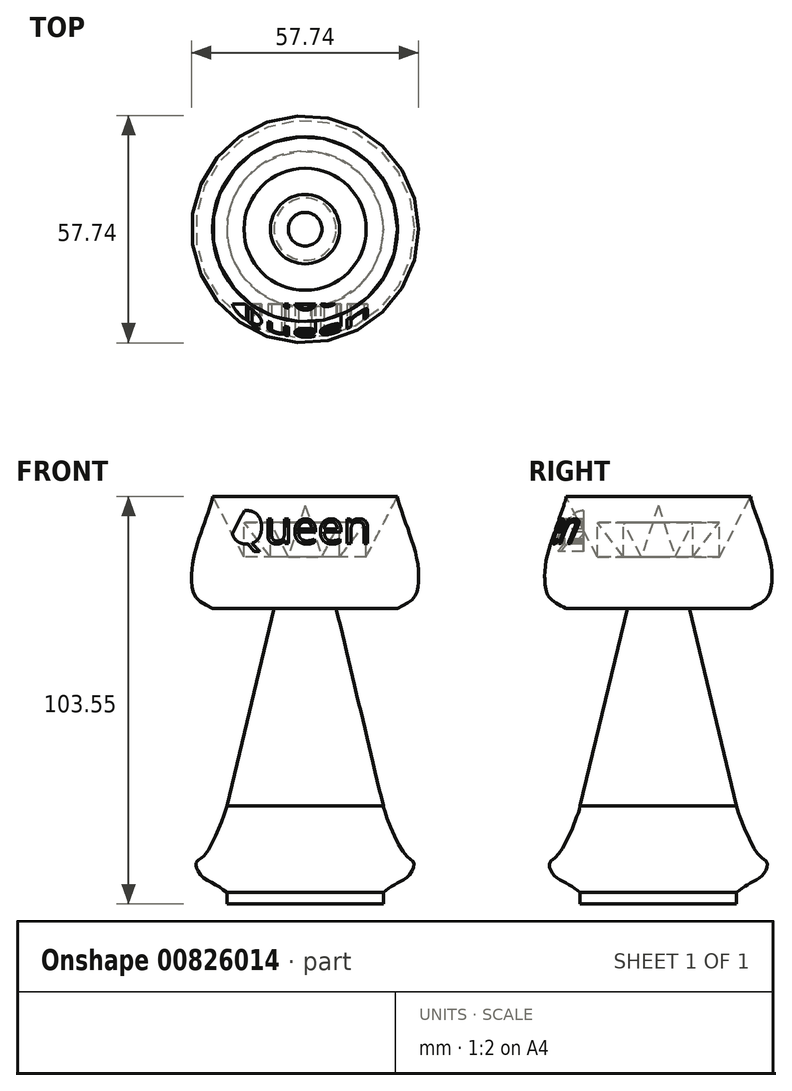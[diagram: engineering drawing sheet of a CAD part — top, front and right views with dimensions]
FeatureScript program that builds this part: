
annotation { "Feature Type Name" : "Feature", "Feature Type Description" : "" }
export const myFeature = defineFeature(function(context is Context, id is Id, definition is map)
    precondition{}
    {
        {
            var Q0;
            Q0=qCreatedBy(makeId("Front.planeOp"),FACE);
            var sketch = newSketch(context, id + "F0", { "sketchPlane" : qUnion([Q0])});
            skLineSegment(sketch, "E0", {"start": v(0, 46) * mm, "end": v(0, -55.25) * mm});
            skLineSegment(sketch, "E1", {"start": v(0, -55.25) * mm, "end": v(19.87, -55.25) * mm});
            skLineSegment(sketch, "E2", {"start": v(19.87, -55.25) * mm, "end": v(19.87, -52.35) * mm});
            skFitSpline(sketch, "E3", {"points": [v(19.87, -52.35) * mm, v(21.86, -50.9) * mm, v(24.04, -49.63) * mm, v(26.58, -47.81) * mm, v(27.67, -44.9) * mm, v(25.31, -42.55) * mm, v(19.87, -30.57) * mm, v(19.87, -30.4) * mm], "startDerivative": vector(15.77, 12.02) * mm, "endDerivative": vector(1.1, 2.52) * mm});
            skLineSegment(sketch, "E4", {"start": v(19.87, -30.4) * mm, "end": v(7.9, 19.87) * mm});
            skLineSegment(sketch, "E5", {"start": v(7.9, 19.87) * mm, "end": v(23.5, 19.87) * mm});
            skFitSpline(sketch, "E6", {"points": [v(23.5, 19.87) * mm, v(27.49, 22.4) * mm, v(28.76, 25.86) * mm, v(28.58, 31.48) * mm, v(26.95, 37.65) * mm, v(24.95, 43.28) * mm, v(23.5, 47.81) * mm, v(23.5, 48.18) * mm, v(23.5, 48.36) * mm], "startDerivative": vector(31.12, 15.03) * mm, "endDerivative": vector(-0.24, 6.22) * mm});
            skLineSegment(sketch, "E7", {"start": v(23.5, 48.3) * mm, "end": v(15.51, 32.93) * mm});
            skLineSegment(sketch, "E8", {"start": v(15.51, 32.93) * mm, "end": v(15.51, 41.64) * mm});
            skLineSegment(sketch, "E9", {"start": v(15.51, 41.64) * mm, "end": v(8.8, 32.93) * mm});
            skLineSegment(sketch, "E10", {"start": v(8.8, 32.93) * mm, "end": v(8.8, 41.64) * mm});
            skLineSegment(sketch, "E11", {"start": v(8.8, 41.64) * mm, "end": v(4.27, 32.93) * mm});
            skLineSegment(sketch, "E12", {"start": v(4.27, 32.93) * mm, "end": v(0, 46) * mm});
            skSolve(sketch);
        }
        {
            var Q0;
            Q0 = qSketchRegion(id + "F0", true);
            var Q1;
            Q1=sQuery(id+"F0.wireOp",EDGE,"E0");
            revolve(context, id + "F1", {"surfaceOperationType" : NewSurfaceOperationType.NEW, "entities" : qUnion([Q0]), "axis" : qUnion([Q1]), "revolveType" : RevolveType.FULL});
        }
        {
            var Q0;
            Q0=qCreatedBy(makeId("Front.planeOp"),FACE);
            cPlane(context, id + "F2", {"entities" : qUnion([Q0]), "cplaneType" : CPlaneType.OFFSET, "offset" : 38.8 * mm, "width" : 150 * mm, "height" : 150 * mm});
        }
        {
            var Q0;
            Q0=qCreatedBy(id+"F2.planeOp",FACE);
            var sketch = newSketch(context, id + "F3", { "sketchPlane" : qUnion([Q0])});
            skText(sketch, "E13", { "text": "Queen", "fontName": "OpenSans-Regular.ttf"});
            const initialGuessF3  = {"E13": [-0.01938, 0.0363, 1, 0, 0.00833]};
            skSetInitialGuess(sketch, initialGuessF3);
            skSolve(sketch);
        }
        {
            var Q0;
            Q0 = qSketchRegion(id + "F3", true);
            var Q1;
            Q1=makeQuery(id+"F3.imprint","IMPRINT",FACE,{"disambiguationData":[TD([[makeQuery(id+"F3.imprint","IMPRINT",EDGE,{"derivedFrom":sQuery(id+"F3.wireOp",EDGE,"E13.sketch_text.stroke-12")}),1.0]])]});
            extrude(context, id + "F4", {"entities" : qUnion([Q0, Q1]), "operationType" : NewBodyOperationType.REMOVE, "oppositeDirection" : true, "depth" : 19.8 * mm, "offsetDistance" : 25 * mm});
        }
    });
